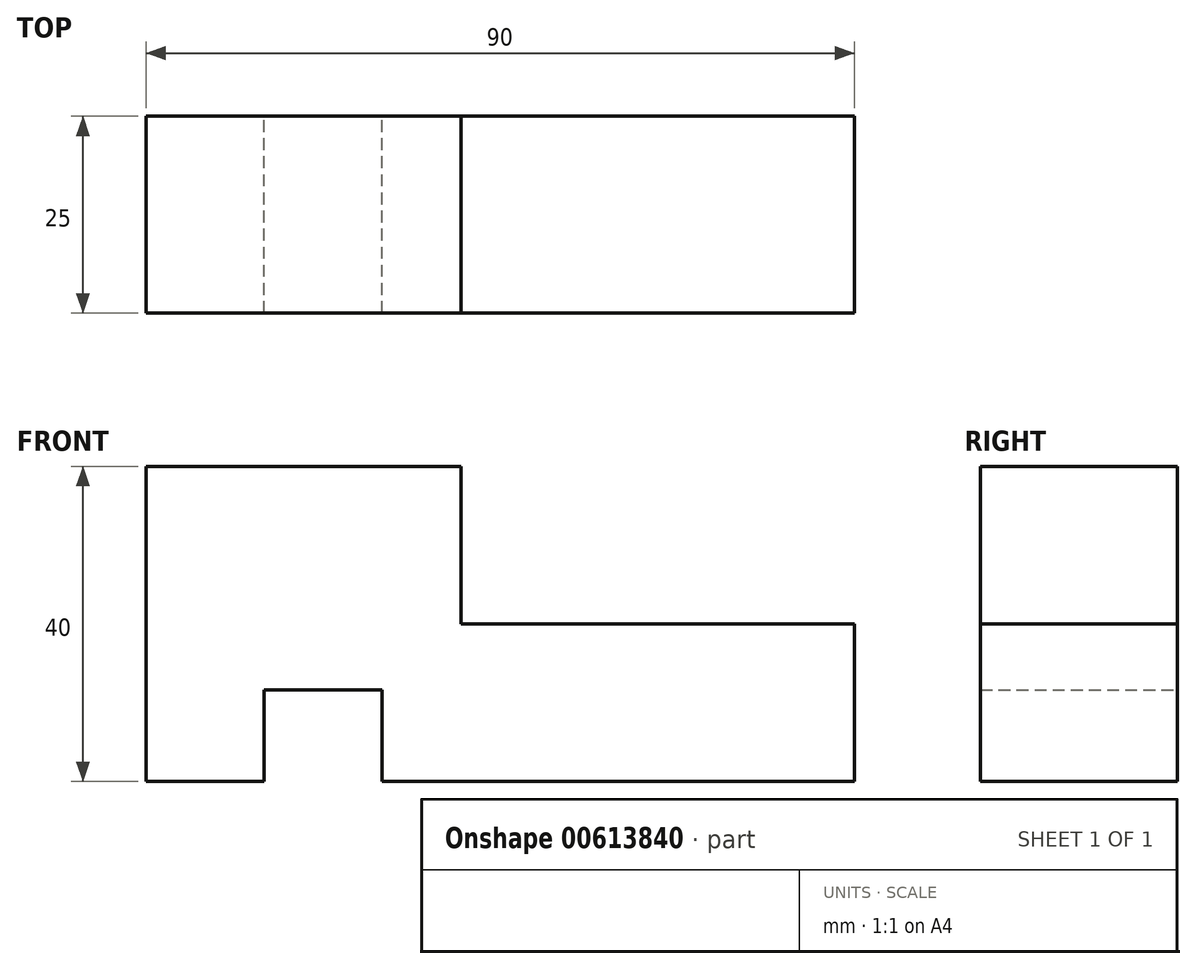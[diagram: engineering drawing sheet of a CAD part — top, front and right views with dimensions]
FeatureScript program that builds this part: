
annotation { "Feature Type Name" : "Feature", "Feature Type Description" : "" }
export const myFeature = defineFeature(function(context is Context, id is Id, definition is map)
    precondition{}
    {
        {
            var Q0;
            Q0=qCreatedBy(makeId("Front.planeOp"),FACE);
            var sketch = newSketch(context, id + "F0", { "sketchPlane" : qUnion([Q0])});
            skLineSegment(sketch, "E0", {"start": v(-68.77, 50.06) * mm, "end": v(-28.77, 50.06) * mm});
            skLineSegment(sketch, "E1", {"start": v(-28.77, 50.06) * mm, "end": v(-28.77, 30.06) * mm});
            skLineSegment(sketch, "E2", {"start": v(-28.77, 30.06) * mm, "end": v(21.23, 30.06) * mm});
            skLineSegment(sketch, "E3", {"start": v(21.23, 30.06) * mm, "end": v(21.23, 10.06) * mm});
            skLineSegment(sketch, "E4", {"start": v(21.23, 10.06) * mm, "end": v(-38.77, 10.06) * mm});
            skLineSegment(sketch, "E5", {"start": v(-38.77, 10.06) * mm, "end": v(-38.77, 21.66) * mm});
            skLineSegment(sketch, "E6", {"start": v(-38.77, 21.66) * mm, "end": v(-53.77, 21.66) * mm});
            skLineSegment(sketch, "E7", {"start": v(-53.77, 21.66) * mm, "end": v(-53.77, 10.06) * mm});
            skLineSegment(sketch, "E8", {"start": v(-53.77, 10.06) * mm, "end": v(-68.77, 10.06) * mm});
            skLineSegment(sketch, "E9", {"start": v(-68.77, 10.06) * mm, "end": v(-68.77, 50.06) * mm});
            skSolve(sketch);
        }
        {
            var Q0;
            Q0 = qSketchRegion(id + "F0", true);
            extrude(context, id + "F1", {"entities" : qUnion([Q0]), "depth" : 25 * mm, "offsetDistance" : 25 * mm});
        }
    });
